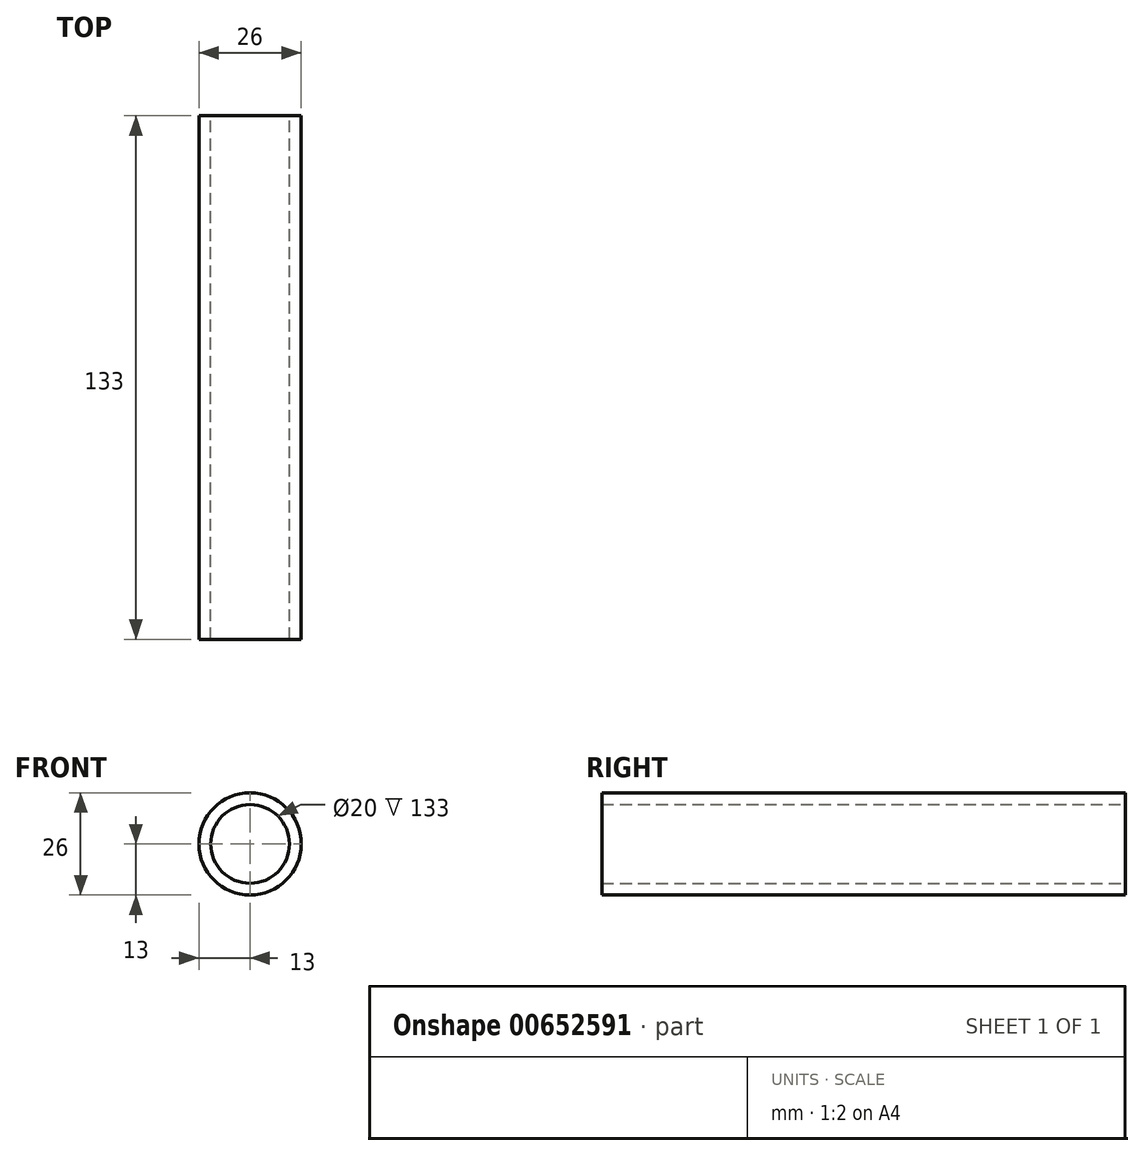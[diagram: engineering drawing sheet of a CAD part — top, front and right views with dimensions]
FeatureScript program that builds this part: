
annotation { "Feature Type Name" : "Feature", "Feature Type Description" : "" }
export const myFeature = defineFeature(function(context is Context, id is Id, definition is map)
    precondition{}
    {
        {
            var Q0;
            Q0=qCreatedBy(makeId("Front.planeOp"),FACE);
            var sketch = newSketch(context, id + "F0", { "sketchPlane" : qUnion([Q0])});
            skCircle(sketch, "E0", {"center": v(0, 0) * mm, "radius": 10 * mm});
            skCircle(sketch, "E1", {"center": v(0, 0) * mm, "radius": 13 * mm});
            skSolve(sketch);
        }
        {
            var Q0;
            Q0 = qSketchRegion(id + "F0", true);
            extrude(context, id + "F1", {"entities" : qUnion([Q0]), "depth" : 133 * mm, "offsetDistance" : 25 * mm});
        }
    });
